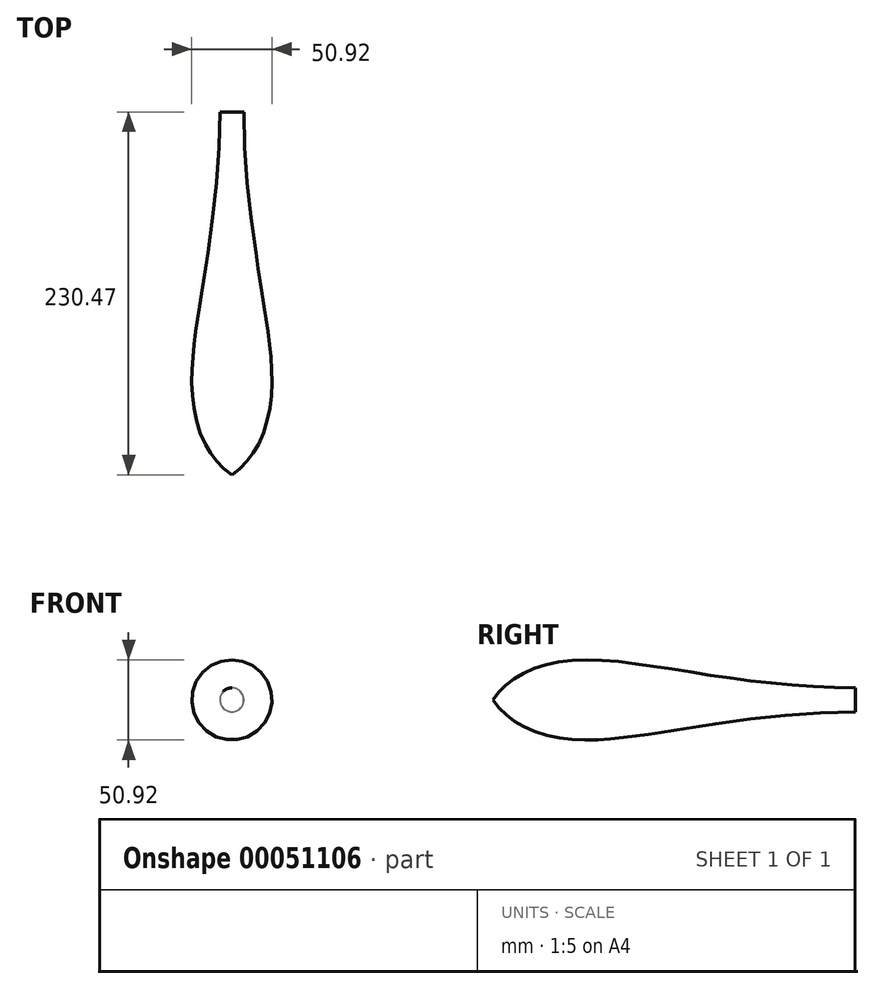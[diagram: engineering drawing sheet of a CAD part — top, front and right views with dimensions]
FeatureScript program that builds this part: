
annotation { "Feature Type Name" : "Feature", "Feature Type Description" : "" }
export const myFeature = defineFeature(function(context is Context, id is Id, definition is map)
    precondition{}
    {
        {
            var Q0;
            Q0=qCreatedBy(makeId("Right.planeOp"),FACE);
            var sketch = newSketch(context, id + "F0", { "sketchPlane" : qUnion([Q0])});
            skLineSegment(sketch, "E0", {"start": v(0, 0) * mm, "end": v(0, 25.4) * mm, "construction": true});
            skLineSegment(sketch, "E1", {"start": v(0, 0) * mm, "end": v(-140.73, 0) * mm, "construction": true});
            skLineSegment(sketch, "E2", {"start": v(0, 0) * mm, "end": v(174.6, 0) * mm, "construction": true});
            skLineSegment(sketch, "E3", {"start": v(174.6, 0) * mm, "end": v(174.6, 7.62) * mm});
            skLineSegment(sketch, "E4", {"start": v(174.6, 7.62) * mm, "end": v(231.32, 7.62) * mm, "construction": true});
            skFitSpline(sketch, "E5", {"points": [v(-55.86, 0) * mm, v(-37.69, 16.18) * mm, v(0, 25.4) * mm, v(71.89, 17.29) * mm, v(174.6, 7.62) * mm], "startDerivative": vector(73.2, 109.13) * mm, "endDerivative": vector(310.26, 0) * mm});
            skSolve(sketch);
        }
        {
            var Q0;
            Q0=sQuery(id+"F0.wireOp",EDGE,"E5");
            var Q1;
            Q1=sQuery(id+"F0.wireOp",EDGE,"E3");
            var Q2;
            Q2=sQuery(id+"F0.wireOp",EDGE,"E2");
            revolve(context, id + "F1", {"bodyType" : ToolBodyType.SURFACE, "surfaceEntities" : qUnion([Q0, Q1]), "axis" : qUnion([Q2]), "revolveType" : RevolveType.FULL});
        }
    });
